annotation { "Feature Type Name" : "Feature", "Feature Type Description" : "" }
export const myFeature = defineFeature(function(context is Context, id is Id, definition is map)
    precondition{}
    {
        {
            var Q0;
            Q0=qCreatedBy(makeId("Top.planeOp"),FACE);
            var sketch = newSketch(context, id + "F0", { "sketchPlane" : qUnion([Q0])});
            skLineSegment(sketch, "E0.bottom", {"start": v(-33, 25.23) * mm, "end": v(32, 25.23) * mm});
            skLineSegment(sketch, "E0.top", {"start": v(-33, -25.27) * mm, "end": v(32, -25.27) * mm});
            skLineSegment(sketch, "E0.left", {"start": v(-33, 25.23) * mm, "end": v(-33, -25.27) * mm});
            skLineSegment(sketch, "E0.right", {"start": v(32, 25.23) * mm, "end": v(32, -25.27) * mm});
            skSolve(sketch);
        }
        {
            var Q0;
            Q0 = qSketchRegion(id + "F0", true);
            extrude(context, id + "F1", {"entities" : qUnion([Q0]), "depth" : 5.5 * mm, "offsetDistance" : 25.4 * mm});
        }
        {
            var Q0;
            Q0=makeQuery(id+"F1.opExtrude","CAP_FACE",FACE,{"disambiguationData":[OSD([sQuery(id+"F0.wireOp",EDGE,"E0.bottom"),sQuery(id+"F0.wireOp",EDGE,"E0.top"),sQuery(id+"F0.wireOp",EDGE,"E0.left"),sQuery(id+"F0.wireOp",EDGE,"E0.right")])],"isStart":false});
            var sketch = newSketch(context, id + "F2", { "sketchPlane" : qUnion([Q0])});
            skLineSegment(sketch, "E1", {"start": v(-25.4, 1.14) * mm, "end": v(-25.4, -9.78) * mm});
            skLineSegment(sketch, "E2", {"start": v(-25.4, -9.78) * mm, "end": v(-18.6, -9.78) * mm});
            skLineSegment(sketch, "E3", {"start": v(-18.6, -9.78) * mm, "end": v(-18.6, -7.24) * mm});
            skLineSegment(sketch, "E4", {"start": v(-18.6, -7.24) * mm, "end": v(-22.3, -7.24) * mm});
            skLineSegment(sketch, "E5", {"start": v(-22.3, -7.24) * mm, "end": v(-22.3, 1.04) * mm});
            skLineSegment(sketch, "E6", {"start": v(-25.4, 1.14) * mm, "end": v(-22.3, 1.14) * mm});
            skLineSegment(sketch, "E7", {"start": v(-22.3, 1.04) * mm, "end": v(-22.3, 1.14) * mm});
            skLineSegment(sketch, "E8", {"start": v(-17.53, -1.87) * mm, "end": v(-17.53, -9.78) * mm});
            skLineSegment(sketch, "E9", {"start": v(-17.53, -9.78) * mm, "end": v(-14.69, -9.78) * mm});
            skLineSegment(sketch, "E10", {"start": v(-14.69, -9.78) * mm, "end": v(-14.69, -1.87) * mm});
            skLineSegment(sketch, "E11", {"start": v(-17.53, -1.87) * mm, "end": v(-14.69, -1.87) * mm});
            skLineSegment(sketch, "E12", {"start": v(-16.63, 1.4) * mm, "end": v(-15.4, 1.4) * mm});
            skLineSegment(sketch, "E13", {"start": v(-15.4, 1.4) * mm, "end": v(-15.08, 1.26) * mm});
            skLineSegment(sketch, "E14", {"start": v(-15.08, 1.26) * mm, "end": v(-14.74, 0.9) * mm});
            skLineSegment(sketch, "E15", {"start": v(-14.74, 0.9) * mm, "end": v(-14.45, 0.5) * mm});
            skLineSegment(sketch, "E16", {"start": v(-14.45, 0.5) * mm, "end": v(-14.45, -0.48) * mm});
            skLineSegment(sketch, "E17", {"start": v(-14.45, -0.48) * mm, "end": v(-14.7, -0.78) * mm});
            skLineSegment(sketch, "E18", {"start": v(-14.7, -0.78) * mm, "end": v(-15.1, -1.06) * mm});
            skLineSegment(sketch, "E19", {"start": v(-15.1, -1.06) * mm, "end": v(-15.4, -1.2) * mm});
            skLineSegment(sketch, "E20", {"start": v(-15.4, -1.2) * mm, "end": v(-16.63, -1.2) * mm});
            skLineSegment(sketch, "E21", {"start": v(-16.63, -1.2) * mm, "end": v(-16.93, -1.06) * mm});
            skLineSegment(sketch, "E22", {"start": v(-16.93, -1.06) * mm, "end": v(-17.33, -0.78) * mm});
            skLineSegment(sketch, "E23", {"start": v(-17.33, -0.78) * mm, "end": v(-17.62, -0.48) * mm});
            skLineSegment(sketch, "E24", {"start": v(-17.62, -0.48) * mm, "end": v(-17.62, 0.5) * mm});
            skLineSegment(sketch, "E25", {"start": v(-17.62, 0.5) * mm, "end": v(-17.43, 0.9) * mm});
            skLineSegment(sketch, "E26", {"start": v(-17.43, 0.9) * mm, "end": v(-17.12, 1.2) * mm});
            skLineSegment(sketch, "E27", {"start": v(-17.12, 1.2) * mm, "end": v(-16.63, 1.4) * mm});
            skLineSegment(sketch, "E28", {"start": v(-13.15, 1.2) * mm, "end": v(-13.15, -9.45) * mm});
            skLineSegment(sketch, "E29", {"start": v(-13.15, -9.45) * mm, "end": v(-12.45, -9.63) * mm});
            skLineSegment(sketch, "E30", {"start": v(-12.45, -9.63) * mm, "end": v(-11.72, -9.96) * mm});
            skLineSegment(sketch, "E31", {"start": v(-11.72, -9.96) * mm, "end": v(-8.41, -9.96) * mm});
            skLineSegment(sketch, "E32", {"start": v(-8.41, -9.96) * mm, "end": v(-7.4, -9.69) * mm});
            skLineSegment(sketch, "E33", {"start": v(-7.4, -9.69) * mm, "end": v(-6.28, -8.93) * mm});
            skLineSegment(sketch, "E34", {"start": v(-6.28, -8.93) * mm, "end": v(-5.49, -7.68) * mm});
            skLineSegment(sketch, "E35", {"start": v(-5.49, -7.68) * mm, "end": v(-5.16, -6.17) * mm});
            skLineSegment(sketch, "E36", {"start": v(-5.16, -6.17) * mm, "end": v(-5.16, -4.8) * mm});
            skLineSegment(sketch, "E37", {"start": v(-5.16, -4.8) * mm, "end": v(-5.63, -3.2) * mm});
            skLineSegment(sketch, "E38", {"start": v(-5.63, -3.2) * mm, "end": v(-6.68, -2.1) * mm});
            skLineSegment(sketch, "E39", {"start": v(-6.68, -2.1) * mm, "end": v(-8.03, -1.75) * mm});
            skLineSegment(sketch, "E40", {"start": v(-8.03, -1.75) * mm, "end": v(-8.99, -1.93) * mm});
            skLineSegment(sketch, "E41", {"start": v(-8.99, -1.93) * mm, "end": v(-10.1, -2.68) * mm});
            skLineSegment(sketch, "E42", {"start": v(-10.1, -2.68) * mm, "end": v(-10.1, 1.2) * mm});
            skLineSegment(sketch, "E43", {"start": v(-10.1, 1.2) * mm, "end": v(-13.15, 1.2) * mm});
            skLineSegment(sketch, "E44", {"start": v(-10.1, -4.43) * mm, "end": v(-10.1, -7.64) * mm});
            skLineSegment(sketch, "E45", {"start": v(-10.1, -7.64) * mm, "end": v(-9.67, -7.83) * mm});
            skLineSegment(sketch, "E46", {"start": v(-9.67, -7.83) * mm, "end": v(-9.15, -7.83) * mm});
            skLineSegment(sketch, "E47", {"start": v(-9.15, -7.83) * mm, "end": v(-8.72, -7.64) * mm});
            skLineSegment(sketch, "E48", {"start": v(-8.72, -7.64) * mm, "end": v(-8.4, -7.24) * mm});
            skLineSegment(sketch, "E49", {"start": v(-8.4, -7.24) * mm, "end": v(-8.18, -6.73) * mm});
            skLineSegment(sketch, "E50", {"start": v(-8.18, -6.73) * mm, "end": v(-8.18, -5.3) * mm});
            skLineSegment(sketch, "E51", {"start": v(-8.18, -5.3) * mm, "end": v(-8.4, -4.83) * mm});
            skLineSegment(sketch, "E52", {"start": v(-8.4, -4.83) * mm, "end": v(-8.75, -4.3) * mm});
            skLineSegment(sketch, "E53", {"start": v(-8.75, -4.3) * mm, "end": v(-9.18, -4.12) * mm});
            skLineSegment(sketch, "E54", {"start": v(-9.18, -4.12) * mm, "end": v(-9.71, -4.22) * mm});
            skLineSegment(sketch, "E55", {"start": v(-9.71, -4.22) * mm, "end": v(-10.1, -4.43) * mm});
            skLineSegment(sketch, "E56", {"start": v(-4.09, -1.93) * mm, "end": v(-4.09, -9.8) * mm});
            skLineSegment(sketch, "E57", {"start": v(-4.09, -9.8) * mm, "end": v(-1.16, -9.8) * mm});
            skLineSegment(sketch, "E58", {"start": v(-1.16, -9.8) * mm, "end": v(-1.16, -4.82) * mm});
            skLineSegment(sketch, "E59", {"start": v(-1.16, -4.82) * mm, "end": v(-0.9, -4.62) * mm});
            skLineSegment(sketch, "E60", {"start": v(-0.9, -4.62) * mm, "end": v(-0.4, -4.44) * mm});
            skLineSegment(sketch, "E61", {"start": v(-0.4, -4.44) * mm, "end": v(1.12, -4.44) * mm});
            skLineSegment(sketch, "E62", {"start": v(1.12, -4.44) * mm, "end": v(1.12, -1.73) * mm});
            skLineSegment(sketch, "E63", {"start": v(1.12, -1.73) * mm, "end": v(0.47, -1.73) * mm});
            skLineSegment(sketch, "E64", {"start": v(0.47, -1.73) * mm, "end": v(-0.46, -2) * mm});
            skLineSegment(sketch, "E65", {"start": v(-0.46, -2) * mm, "end": v(-0.98, -2.4) * mm});
            skLineSegment(sketch, "E66", {"start": v(-0.98, -2.4) * mm, "end": v(-1.41, -2.86) * mm});
            skLineSegment(sketch, "E67", {"start": v(-1.41, -2.86) * mm, "end": v(-1.7, -1.9) * mm});
            skLineSegment(sketch, "E68", {"start": v(-1.7, -1.9) * mm, "end": v(-4.09, -1.93) * mm});
            skLineSegment(sketch, "E69", {"start": v(1.95, -2.42) * mm, "end": v(2.47, -4.64) * mm});
            skLineSegment(sketch, "E70", {"start": v(2.47, -4.64) * mm, "end": v(2.71, -4.45) * mm});
            skLineSegment(sketch, "E71", {"start": v(2.71, -4.45) * mm, "end": v(3.25, -4.21) * mm});
            skLineSegment(sketch, "E72", {"start": v(3.25, -4.21) * mm, "end": v(4.03, -4.03) * mm});
            skLineSegment(sketch, "E73", {"start": v(4.03, -4.03) * mm, "end": v(5.37, -4.03) * mm});
            skLineSegment(sketch, "E74", {"start": v(5.37, -4.03) * mm, "end": v(5.71, -4.28) * mm});
            skLineSegment(sketch, "E75", {"start": v(5.71, -4.28) * mm, "end": v(5.88, -4.58) * mm});
            skLineSegment(sketch, "E76", {"start": v(5.88, -4.58) * mm, "end": v(5.88, -5.06) * mm});
            skLineSegment(sketch, "E77", {"start": v(5.88, -5.06) * mm, "end": v(5.05, -5.06) * mm});
            skLineSegment(sketch, "E78", {"start": v(5.05, -5.06) * mm, "end": v(3.95, -5.21) * mm});
            skLineSegment(sketch, "E79", {"start": v(3.95, -5.21) * mm, "end": v(2.89, -5.64) * mm});
            skLineSegment(sketch, "E80", {"start": v(2.89, -5.64) * mm, "end": v(1.78, -6.56) * mm});
            skLineSegment(sketch, "E81", {"start": v(1.78, -6.56) * mm, "end": v(1.49, -7.15) * mm});
            skLineSegment(sketch, "E82", {"start": v(1.49, -7.15) * mm, "end": v(1.49, -8.3) * mm});
            skLineSegment(sketch, "E83", {"start": v(1.49, -8.3) * mm, "end": v(1.78, -8.9) * mm});
            skLineSegment(sketch, "E84", {"start": v(1.78, -8.9) * mm, "end": v(2.29, -9.43) * mm});
            skLineSegment(sketch, "E85", {"start": v(2.29, -9.43) * mm, "end": v(3.16, -9.9) * mm});
            skLineSegment(sketch, "E86", {"start": v(3.16, -9.9) * mm, "end": v(4.03, -10.08) * mm});
            skLineSegment(sketch, "E87", {"start": v(4.03, -10.08) * mm, "end": v(5.06, -9.95) * mm});
            skLineSegment(sketch, "E88", {"start": v(5.06, -9.95) * mm, "end": v(5.74, -9.58) * mm});
            skLineSegment(sketch, "E89", {"start": v(5.74, -9.58) * mm, "end": v(6.46, -8.97) * mm});
            skLineSegment(sketch, "E90", {"start": v(6.46, -8.97) * mm, "end": v(6.57, -9.38) * mm});
            skLineSegment(sketch, "E91", {"start": v(6.57, -9.38) * mm, "end": v(6.57, -9.93) * mm});
            skLineSegment(sketch, "E92", {"start": v(6.57, -9.93) * mm, "end": v(8.93, -9.93) * mm});
            skLineSegment(sketch, "E93", {"start": v(8.93, -9.93) * mm, "end": v(8.93, -3.86) * mm});
            skLineSegment(sketch, "E94", {"start": v(8.93, -3.86) * mm, "end": v(8.8, -3.24) * mm});
            skLineSegment(sketch, "E95", {"start": v(8.8, -3.24) * mm, "end": v(8.47, -2.65) * mm});
            skLineSegment(sketch, "E96", {"start": v(8.47, -2.65) * mm, "end": v(7.83, -2.24) * mm});
            skLineSegment(sketch, "E97", {"start": v(7.83, -2.24) * mm, "end": v(7.12, -1.9) * mm});
            skLineSegment(sketch, "E98", {"start": v(7.12, -1.9) * mm, "end": v(6.2, -1.76) * mm});
            skLineSegment(sketch, "E99", {"start": v(6.2, -1.76) * mm, "end": v(4.23, -1.76) * mm});
            skLineSegment(sketch, "E100", {"start": v(4.23, -1.76) * mm, "end": v(3.41, -1.9) * mm});
            skLineSegment(sketch, "E101", {"start": v(3.41, -1.9) * mm, "end": v(2.4, -2.18) * mm});
            skLineSegment(sketch, "E102", {"start": v(2.4, -2.18) * mm, "end": v(1.95, -2.42) * mm});
            skLineSegment(sketch, "E103", {"start": v(6.03, -6.8) * mm, "end": v(6.03, -7.77) * mm});
            skLineSegment(sketch, "E104", {"start": v(6.03, -7.77) * mm, "end": v(5.53, -7.96) * mm});
            skLineSegment(sketch, "E105", {"start": v(5.53, -7.96) * mm, "end": v(4.86, -7.96) * mm});
            skLineSegment(sketch, "E106", {"start": v(4.86, -7.96) * mm, "end": v(4.6, -7.74) * mm});
            skLineSegment(sketch, "E107", {"start": v(4.6, -7.74) * mm, "end": v(4.6, -7.1) * mm});
            skLineSegment(sketch, "E108", {"start": v(4.6, -7.1) * mm, "end": v(4.9, -6.85) * mm});
            skLineSegment(sketch, "E109", {"start": v(4.9, -6.85) * mm, "end": v(5.88, -6.85) * mm});
            skLineSegment(sketch, "E110", {"start": v(5.88, -6.85) * mm, "end": v(6.03, -7.1) * mm});
            skLineSegment(sketch, "E111", {"start": v(10.35, -1.98) * mm, "end": v(10.35, -9.84) * mm});
            skLineSegment(sketch, "E112", {"start": v(10.35, -9.84) * mm, "end": v(13.28, -9.84) * mm});
            skLineSegment(sketch, "E113", {"start": v(13.28, -9.84) * mm, "end": v(13.28, -4.87) * mm});
            skLineSegment(sketch, "E114", {"start": v(13.28, -4.87) * mm, "end": v(13.55, -4.67) * mm});
            skLineSegment(sketch, "E115", {"start": v(13.55, -4.67) * mm, "end": v(14.03, -4.49) * mm});
            skLineSegment(sketch, "E116", {"start": v(14.03, -4.49) * mm, "end": v(15.56, -4.49) * mm});
            skLineSegment(sketch, "E117", {"start": v(15.56, -4.49) * mm, "end": v(15.56, -1.78) * mm});
            skLineSegment(sketch, "E118", {"start": v(15.56, -1.78) * mm, "end": v(14.91, -1.78) * mm});
            skLineSegment(sketch, "E119", {"start": v(14.91, -1.78) * mm, "end": v(13.98, -2.05) * mm});
            skLineSegment(sketch, "E120", {"start": v(13.98, -2.05) * mm, "end": v(13.46, -2.44) * mm});
            skLineSegment(sketch, "E121", {"start": v(13.46, -2.44) * mm, "end": v(13.03, -2.9) * mm});
            skLineSegment(sketch, "E122", {"start": v(13.03, -2.9) * mm, "end": v(12.74, -1.94) * mm});
            skLineSegment(sketch, "E123", {"start": v(12.74, -1.94) * mm, "end": v(10.35, -1.98) * mm});
            skLineSegment(sketch, "E124", {"start": v(16.07, -1.85) * mm, "end": v(19.2, -1.85) * mm});
            skLineSegment(sketch, "E125", {"start": v(19.2, -1.85) * mm, "end": v(20.27, -7.49) * mm});
            skLineSegment(sketch, "E126", {"start": v(20.27, -7.49) * mm, "end": v(21.54, -1.85) * mm});
            skLineSegment(sketch, "E127", {"start": v(21.54, -1.85) * mm, "end": v(24.54, -1.85) * mm});
            skLineSegment(sketch, "E128", {"start": v(24.54, -1.85) * mm, "end": v(21.42, -10.85) * mm});
            skLineSegment(sketch, "E129", {"start": v(21.42, -10.85) * mm, "end": v(20.95, -11.62) * mm});
            skLineSegment(sketch, "E130", {"start": v(20.95, -11.62) * mm, "end": v(20.2, -12.3) * mm});
            skLineSegment(sketch, "E131", {"start": v(20.2, -12.3) * mm, "end": v(19.34, -12.78) * mm});
            skLineSegment(sketch, "E132", {"start": v(19.34, -12.78) * mm, "end": v(19.2, -12.85) * mm});
            skLineSegment(sketch, "E133", {"start": v(19.2, -12.85) * mm, "end": v(17.93, -12.98) * mm});
            skLineSegment(sketch, "E134", {"start": v(17.93, -12.98) * mm, "end": v(16.38, -12.85) * mm});
            skLineSegment(sketch, "E135", {"start": v(16.38, -12.85) * mm, "end": v(16.56, -10.64) * mm});
            skLineSegment(sketch, "E136", {"start": v(16.56, -10.64) * mm, "end": v(16.87, -10.84) * mm});
            skLineSegment(sketch, "E137", {"start": v(16.87, -10.84) * mm, "end": v(17.08, -10.96) * mm});
            skLineSegment(sketch, "E138", {"start": v(17.08, -10.96) * mm, "end": v(17.78, -10.96) * mm});
            skLineSegment(sketch, "E139", {"start": v(17.78, -10.96) * mm, "end": v(18.23, -10.7) * mm});
            skLineSegment(sketch, "E140", {"start": v(18.23, -10.7) * mm, "end": v(18.54, -10.35) * mm});
            skLineSegment(sketch, "E141", {"start": v(18.54, -10.35) * mm, "end": v(18.76, -10.06) * mm});
            skLineSegment(sketch, "E142", {"start": v(18.76, -10.06) * mm, "end": v(16.07, -1.85) * mm});
            skLineSegment(sketch, "E143", {"start": v(8.07, 18.08) * mm, "end": v(5.06, 11.22) * mm});
            skLineSegment(sketch, "E144", {"start": v(5.06, 11.22) * mm, "end": v(1.82, 11.82) * mm});
            skLineSegment(sketch, "E145", {"start": v(1.82, 11.82) * mm, "end": v(7.55, 17.56) * mm});
            skLineSegment(sketch, "E146", {"start": v(7.55, 17.56) * mm, "end": v(0.96, 11.94) * mm});
            skLineSegment(sketch, "E147", {"start": v(0.96, 11.94) * mm, "end": v(-1.24, 12.35) * mm});
            skLineSegment(sketch, "E148", {"start": v(-1.24, 12.35) * mm, "end": v(8.07, 18.08) * mm});
            skLineSegment(sketch, "E149", {"start": v(1.64, 11.39) * mm, "end": v(3.36, 11.07) * mm});
            skLineSegment(sketch, "E150", {"start": v(3.36, 11.07) * mm, "end": v(2.4, 9.56) * mm});
            skLineSegment(sketch, "E151", {"start": v(2.4, 9.56) * mm, "end": v(1.64, 11.39) * mm});
            skLineSegment(sketch, "E152.bottom", {"start": v(-25.43, 10.13) * mm, "end": v(-24.53, 10.13) * mm});
            skLineSegment(sketch, "E152.top", {"start": v(-25.43, 9.88) * mm, "end": v(-24.53, 9.88) * mm});
            skLineSegment(sketch, "E152.left", {"start": v(-25.43, 10.13) * mm, "end": v(-25.43, 9.88) * mm});
            skLineSegment(sketch, "E152.right", {"start": v(-24.53, 10.13) * mm, "end": v(-24.53, 9.88) * mm});
            skLineSegment(sketch, "E153", {"start": v(-23.55, 10.16) * mm, "end": v(-23.55, 9.81) * mm});
            skLineSegment(sketch, "E154", {"start": v(-23.55, 9.81) * mm, "end": v(-22.6, 9.81) * mm});
            skLineSegment(sketch, "E155", {"start": v(-22.6, 9.81) * mm, "end": v(-22.6, 10.14) * mm});
            skLineSegment(sketch, "E156", {"start": v(-22.6, 10.14) * mm, "end": v(-23.55, 10.16) * mm});
            skLineSegment(sketch, "E157", {"start": v(-21.75, 9.83) * mm, "end": v(-21.75, 9.5) * mm});
            skLineSegment(sketch, "E158", {"start": v(-21.75, 9.5) * mm, "end": v(-20.84, 9.12) * mm});
            skLineSegment(sketch, "E159", {"start": v(-20.84, 9.12) * mm, "end": v(-20.84, 9.52) * mm});
            skLineSegment(sketch, "E160", {"start": v(-20.84, 9.52) * mm, "end": v(-21.75, 9.83) * mm});
            skLineSegment(sketch, "E161", {"start": v(-20.03, 9.1) * mm, "end": v(-20.03, 8.7) * mm});
            skLineSegment(sketch, "E162", {"start": v(-20.03, 8.7) * mm, "end": v(-19.44, 8.22) * mm});
            skLineSegment(sketch, "E163", {"start": v(-19.44, 8.22) * mm, "end": v(-19.1, 8.5) * mm});
            skLineSegment(sketch, "E164", {"start": v(-19.1, 8.5) * mm, "end": v(-20.03, 9.1) * mm});
            skLineSegment(sketch, "E165", {"start": v(-18.81, 7.68) * mm, "end": v(-18.52, 7.93) * mm});
            skLineSegment(sketch, "E166", {"start": v(-18.52, 7.93) * mm, "end": v(-17.78, 7.16) * mm});
            skLineSegment(sketch, "E167", {"start": v(-17.78, 7.16) * mm, "end": v(-18.03, 6.93) * mm});
            skLineSegment(sketch, "E168", {"start": v(-18.03, 6.93) * mm, "end": v(-18.81, 7.68) * mm});
            skLineSegment(sketch, "E169", {"start": v(-17.48, 6.32) * mm, "end": v(-17.2, 6.6) * mm});
            skLineSegment(sketch, "E170", {"start": v(-17.2, 6.6) * mm, "end": v(-16.36, 5.9) * mm});
            skLineSegment(sketch, "E171", {"start": v(-16.36, 5.9) * mm, "end": v(-16.67, 5.53) * mm});
            skLineSegment(sketch, "E172", {"start": v(-16.67, 5.53) * mm, "end": v(-17.48, 6.32) * mm});
            skLineSegment(sketch, "E173", {"start": v(-15.72, 5.4) * mm, "end": v(-16.02, 5.12) * mm});
            skLineSegment(sketch, "E174", {"start": v(-16.02, 5.12) * mm, "end": v(-15.14, 4.5) * mm});
            skLineSegment(sketch, "E175", {"start": v(-15.14, 4.5) * mm, "end": v(-14.94, 4.78) * mm});
            skLineSegment(sketch, "E176", {"start": v(-14.94, 4.78) * mm, "end": v(-15.72, 5.4) * mm});
            skLineSegment(sketch, "E177", {"start": v(-14.23, 4.56) * mm, "end": v(-14.23, 4.18) * mm});
            skLineSegment(sketch, "E178", {"start": v(-14.23, 4.18) * mm, "end": v(-13.29, 3.9) * mm});
            skLineSegment(sketch, "E179", {"start": v(-13.29, 3.9) * mm, "end": v(-13.29, 4.25) * mm});
            skLineSegment(sketch, "E180", {"start": v(-13.29, 4.25) * mm, "end": v(-14.23, 4.56) * mm});
            skLineSegment(sketch, "E181", {"start": v(-12.35, 3.84) * mm, "end": v(-11.32, 3.84) * mm});
            skLineSegment(sketch, "E182", {"start": v(-11.32, 3.84) * mm, "end": v(-11.32, 4.27) * mm});
            skLineSegment(sketch, "E183", {"start": v(-9.62, 4.56) * mm, "end": v(-9.83, 4.78) * mm});
            skLineSegment(sketch, "E184", {"start": v(-9.83, 4.78) * mm, "end": v(-10.6, 4.47) * mm});
            skLineSegment(sketch, "E185", {"start": v(-8.58, 6.16) * mm, "end": v(-9.22, 5.54) * mm});
            skLineSegment(sketch, "E186", {"start": v(-9.22, 5.54) * mm, "end": v(-8.86, 5.26) * mm});
            skLineSegment(sketch, "E187", {"start": v(-8.86, 5.26) * mm, "end": v(-8.2, 5.89) * mm});
            skLineSegment(sketch, "E188", {"start": v(-8.2, 5.89) * mm, "end": v(-8.58, 6.16) * mm});
            skLineSegment(sketch, "E189", {"start": v(-7.56, 5.7) * mm, "end": v(-7.56, 5.29) * mm});
            skLineSegment(sketch, "E190", {"start": v(-7.56, 5.29) * mm, "end": v(-6.54, 5.29) * mm});
            skLineSegment(sketch, "E191", {"start": v(-6.54, 5.29) * mm, "end": v(-6.54, 5.7) * mm});
            skLineSegment(sketch, "E192", {"start": v(-6.54, 5.7) * mm, "end": v(-7.56, 5.7) * mm});
            skLineSegment(sketch, "E193", {"start": v(-4.94, 6.06) * mm, "end": v(-5.74, 5.79) * mm});
            skLineSegment(sketch, "E194", {"start": v(-5.74, 5.79) * mm, "end": v(-5.74, 5.4) * mm});
            skLineSegment(sketch, "E195", {"start": v(-5.74, 5.4) * mm, "end": v(-4.84, 5.7) * mm});
            skLineSegment(sketch, "E196", {"start": v(-4.84, 5.7) * mm, "end": v(-4.94, 6.06) * mm});
            skLineSegment(sketch, "E197", {"start": v(-7.7, 7.78) * mm, "end": v(-8.08, 6.98) * mm});
            skLineSegment(sketch, "E198", {"start": v(-8.08, 6.98) * mm, "end": v(-7.7, 6.8) * mm});
            skLineSegment(sketch, "E199", {"start": v(-7.7, 6.8) * mm, "end": v(-7.28, 7.68) * mm});
            skLineSegment(sketch, "E200", {"start": v(-7.28, 7.68) * mm, "end": v(-7.7, 7.78) * mm});
            skLineSegment(sketch, "E201", {"start": v(-10.78, 6.4) * mm, "end": v(-10.38, 6.65) * mm});
            skLineSegment(sketch, "E202", {"start": v(-10.38, 6.65) * mm, "end": v(-9.7, 6.06) * mm});
            skLineSegment(sketch, "E203", {"start": v(-9.7, 6.06) * mm, "end": v(-9.97, 5.75) * mm});
            skLineSegment(sketch, "E204", {"start": v(-9.97, 5.75) * mm, "end": v(-10.78, 6.4) * mm});
            skLineSegment(sketch, "E205", {"start": v(-7.04, 9.56) * mm, "end": v(-7.37, 8.7) * mm});
            skLineSegment(sketch, "E206", {"start": v(-7.37, 8.7) * mm, "end": v(-7, 8.53) * mm});
            skLineSegment(sketch, "E207", {"start": v(-7, 8.53) * mm, "end": v(-6.62, 9.41) * mm});
            skLineSegment(sketch, "E208", {"start": v(-6.62, 9.41) * mm, "end": v(-7.04, 9.56) * mm});
            skLineSegment(sketch, "E209", {"start": v(-6.92, 11.45) * mm, "end": v(-6.92, 10.48) * mm});
            skLineSegment(sketch, "E210", {"start": v(-6.92, 10.48) * mm, "end": v(-6.51, 10.48) * mm});
            skLineSegment(sketch, "E211", {"start": v(-6.51, 10.48) * mm, "end": v(-6.51, 11.43) * mm});
            skLineSegment(sketch, "E212", {"start": v(-6.51, 11.43) * mm, "end": v(-6.92, 11.45) * mm});
            skLineSegment(sketch, "E213", {"start": v(-12.17, 7.68) * mm, "end": v(-11.92, 7.93) * mm});
            skLineSegment(sketch, "E214", {"start": v(-11.92, 7.93) * mm, "end": v(-11.19, 7.16) * mm});
            skLineSegment(sketch, "E215", {"start": v(-11.19, 7.16) * mm, "end": v(-11.46, 6.9) * mm});
            skLineSegment(sketch, "E216", {"start": v(-11.46, 6.9) * mm, "end": v(-12.17, 7.68) * mm});
            skLineSegment(sketch, "E217", {"start": v(-13.1, 9.38) * mm, "end": v(-12.8, 9.56) * mm});
            skLineSegment(sketch, "E218", {"start": v(-12.8, 9.56) * mm, "end": v(-12.27, 8.7) * mm});
            skLineSegment(sketch, "E219", {"start": v(-12.27, 8.7) * mm, "end": v(-12.64, 8.52) * mm});
            skLineSegment(sketch, "E220", {"start": v(-12.64, 8.52) * mm, "end": v(-13.1, 9.38) * mm});
            skLineSegment(sketch, "E221", {"start": v(-3.2, 6.74) * mm, "end": v(-4, 6.24) * mm});
            skLineSegment(sketch, "E222", {"start": v(-4, 6.24) * mm, "end": v(-3.7, 5.95) * mm});
            skLineSegment(sketch, "E223", {"start": v(-3.7, 5.95) * mm, "end": v(-2.96, 6.4) * mm});
            skLineSegment(sketch, "E224", {"start": v(-2.96, 6.4) * mm, "end": v(-3.2, 6.74) * mm});
            skLineSegment(sketch, "E225", {"start": v(-1.65, 7.78) * mm, "end": v(-2.4, 7.16) * mm});
            skLineSegment(sketch, "E226", {"start": v(-2.4, 7.16) * mm, "end": v(-2.12, 6.88) * mm});
            skLineSegment(sketch, "E227", {"start": v(-2.12, 6.88) * mm, "end": v(-1.38, 7.54) * mm});
            skLineSegment(sketch, "E228", {"start": v(-1.38, 7.54) * mm, "end": v(-1.65, 7.78) * mm});
            skLineSegment(sketch, "E229", {"start": v(0.29, 10.33) * mm, "end": v(0.15, 9.83) * mm});
            skLineSegment(sketch, "E230", {"start": v(0.15, 9.83) * mm, "end": v(0.45, 9.74) * mm});
            skLineSegment(sketch, "E231", {"start": v(0.45, 9.74) * mm, "end": v(0.57, 10.16) * mm});
            skLineSegment(sketch, "E232", {"start": v(0.57, 10.16) * mm, "end": v(0.29, 10.33) * mm});
            skLineSegment(sketch, "E233", {"start": v(-0.41, 9.1) * mm, "end": v(-1.03, 8.5) * mm});
            skLineSegment(sketch, "E234", {"start": v(-1.03, 8.5) * mm, "end": v(-0.7, 8.17) * mm});
            skLineSegment(sketch, "E235", {"start": v(-0.7, 8.17) * mm, "end": v(-0.05, 8.8) * mm});
            skLineSegment(sketch, "E236", {"start": v(-0.05, 8.8) * mm, "end": v(-0.41, 9.1) * mm});
            skLineSegment(sketch, "E237", {"start": v(-13.4, 11.26) * mm, "end": v(-13.1, 11.26) * mm});
            skLineSegment(sketch, "E238", {"start": v(-13.1, 11.26) * mm, "end": v(-12.9, 10.33) * mm});
            skLineSegment(sketch, "E239", {"start": v(-12.9, 10.33) * mm, "end": v(-13.24, 10.27) * mm});
            skLineSegment(sketch, "E240", {"start": v(-13.24, 10.27) * mm, "end": v(-13.4, 11.22) * mm});
            skLineSegment(sketch, "E241", {"start": v(-13.4, 11.22) * mm, "end": v(-13.4, 11.26) * mm});
            skLineSegment(sketch, "E242", {"start": v(-12.95, 13.1) * mm, "end": v(-13.31, 12.3) * mm});
            skLineSegment(sketch, "E243", {"start": v(-13.31, 12.3) * mm, "end": v(-12.98, 12.15) * mm});
            skLineSegment(sketch, "E244", {"start": v(-12.98, 12.15) * mm, "end": v(-12.6, 13) * mm});
            skLineSegment(sketch, "E245", {"start": v(-12.6, 13) * mm, "end": v(-12.95, 13.1) * mm});
            skLineSegment(sketch, "E246", {"start": v(-12.34, 13.96) * mm, "end": v(-12.05, 13.65) * mm});
            skLineSegment(sketch, "E247", {"start": v(-12.05, 13.65) * mm, "end": v(-11.3, 14.2) * mm});
            skLineSegment(sketch, "E248", {"start": v(-11.3, 14.2) * mm, "end": v(-11.61, 14.45) * mm});
            skLineSegment(sketch, "E249", {"start": v(-11.61, 14.45) * mm, "end": v(-12.34, 13.96) * mm});
            skLineSegment(sketch, "E250", {"start": v(-10.54, 14.79) * mm, "end": v(-10.54, 14.25) * mm});
            skLineSegment(sketch, "E251", {"start": v(-10.54, 14.25) * mm, "end": v(-9.49, 14.25) * mm});
            skLineSegment(sketch, "E252", {"start": v(-9.49, 14.25) * mm, "end": v(-9.49, 14.78) * mm});
            skLineSegment(sketch, "E253", {"start": v(-9.49, 14.78) * mm, "end": v(-10.54, 14.79) * mm});
            skLineSegment(sketch, "E254", {"start": v(-8.74, 14.27) * mm, "end": v(-8.44, 14.54) * mm});
            skLineSegment(sketch, "E255", {"start": v(-8.44, 14.54) * mm, "end": v(-7.74, 14.06) * mm});
            skLineSegment(sketch, "E256", {"start": v(-7.74, 14.06) * mm, "end": v(-8, 13.8) * mm});
            skLineSegment(sketch, "E257", {"start": v(-8, 13.8) * mm, "end": v(-8.74, 14.27) * mm});
            skLineSegment(sketch, "E258", {"start": v(-7.4, 13.1) * mm, "end": v(-7.1, 13.27) * mm});
            skLineSegment(sketch, "E259", {"start": v(-7.1, 13.27) * mm, "end": v(-6.7, 12.5) * mm});
            skLineSegment(sketch, "E260", {"start": v(-6.7, 12.5) * mm, "end": v(-6.96, 12.27) * mm});
            skLineSegment(sketch, "E261", {"start": v(-6.96, 12.27) * mm, "end": v(-7.4, 13.1) * mm});
            skText(sketch, "E262", { "text": "Bozeman Public", "fontName": "OpenSans-Regular.ttf"});
            skLineSegment(sketch, "E263", {"start": v(-10.6, 4.47) * mm, "end": v(-10.28, 4) * mm});
            skLineSegment(sketch, "E264", {"start": v(-10.28, 4) * mm, "end": v(-9.62, 4.56) * mm});
            skPoint(sketch, "E265.end.orphan", {"position": v(-10.38, 2.85) * mm});
            skPoint(sketch, "E266.start.orphan", {"position": v(-12.35, 2.85) * mm});
            skLineSegment(sketch, "E267", {"start": v(-12.35, 3.84) * mm, "end": v(-12.35, 4.3) * mm});
            skLineSegment(sketch, "E268", {"start": v(-12.35, 4.3) * mm, "end": v(-11.32, 4.27) * mm});
            const initialGuessF2  = {"E262": [-0.00634, 0, 1, 0, 0.00285]};
            skSetInitialGuess(sketch, initialGuessF2);
            skSolve(sketch);
        }
        {
            var Q0;
            Q0 = qSketchRegion(id + "F2", true);
            var Q1;
            Q1 = qSketchRegion(id + "FlI2vZRWEY4i2kz_1", true);
            extrude(context, id + "F3", {"entities" : qUnion([Q0, Q1]), "operationType" : NewBodyOperationType.ADD, "depth" : 3 * mm, "offsetDistance" : 25.4 * mm});
        }
    });